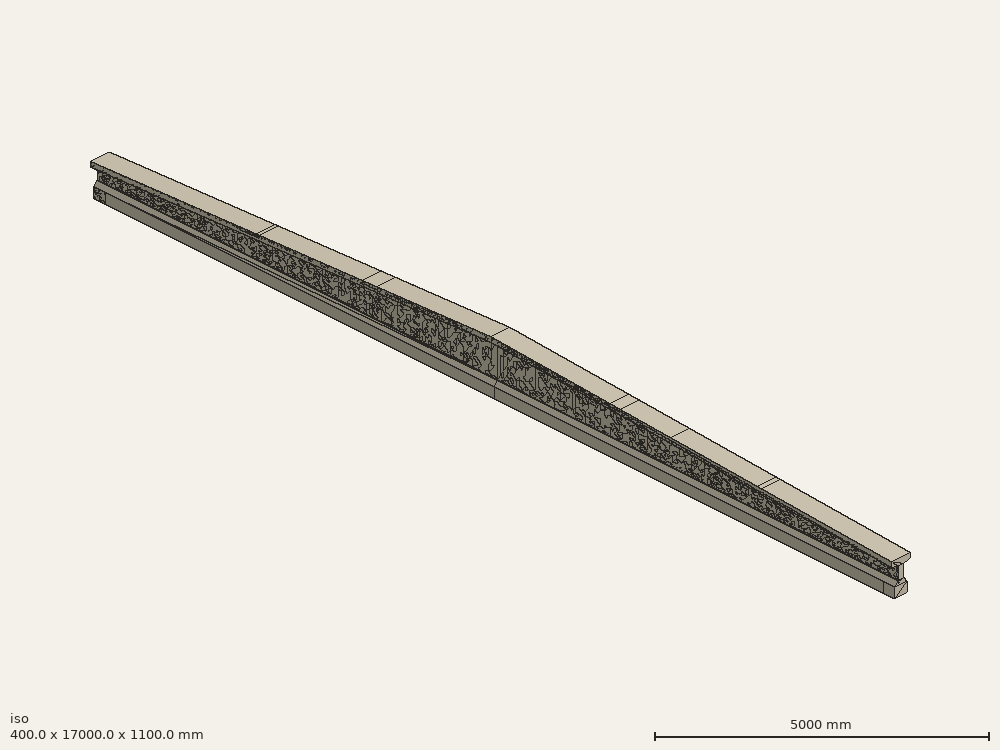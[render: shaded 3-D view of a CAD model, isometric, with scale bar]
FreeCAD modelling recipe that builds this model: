
FCSTD DOCUMENT  (FreeCAD 0.21R33694 (Git))
Label: LGH_3002_beam_2
License: All rights reserved
LicenseURL: http://en.wikipedia.org/wiki/All_rights_reserved
objects: Part::FeaturePython×14, Part::Feature×13, Part::Part2DObjectPython×8, App::MaterialObjectPython×4, Sketcher::SketchObject×3, Part::Compound×2, Fem::ConstraintDisplacement×2, Fem::ConstraintForce×2, Fem::FemSolverObjectPython×1, Part::Loft×1, Part::Extrusion×1, Part::Plane×1, Fem::FemMeshObjectPython×1, Fem::FemAnalysis×1
note: 43 computed .brp shape members not serialized (recipe doc carries the construction recipe); baked Part::Feature solids carry a one-line shape summary decoded from their .brp

FEATURE [Fem::FemSolverObjectPython] SolverCcxTools  # FEM object (typed FeaturePython)
  AnalysisType = 0
  BeamShellResultOutput3D = true
  BucklingFactors = 1
  EigenmodeHighLimit = 1000000
  EigenmodeLowLimit = 0
  EigenmodesCount = 10
  GeometricalNonlinearity = 0
  IterationsControlParameterCutb = 0.25,0.5,0.75,0.85,,,1.5,
  IterationsControlParameterIter = 4,8,9,200,10,400,,200,,
  IterationsControlParameterTimeUse = false
  IterationsThermoMechMaximum = 2000
  IterationsUserDefinedIncrementations = false
  IterationsUserDefinedTimeStepLength = false
  MaterialNonlinearity = 0
  MatrixSolverType = 0
  SplitInputWriter = true
  ThermoMechSteadyState = true
  TimeEnd = 1
  TimeInitialStep = 0.01
FEATURE [Part::Feature] Solid002  label="pad2"
  shape: bbox 400 x 8500 x 530 mm, 6 faces (baked)
FEATURE [Part::Feature] Solid003  label="pad1"
  shape: bbox 400 x 8500 x 530 mm, 6 faces (baked)
FEATURE [Part::Feature] Solid006  label="pad3"
  shape: bbox 400 x 8500 x 530 mm, 6 faces (baked)
FEATURE [Part::Feature] Solid007  label="pad4"
  shape: bbox 400 x 8500 x 530 mm, 6 faces (baked)
FEATURE [Part::Part2DObjectPython] Line  # Draft 2D object (typed FeaturePython)
  Area = 0
  ChamferSize = 0
  Closed = false
  End = (60,8500,970)
  FilletRadius = 0
  Length = 120
  MakeFace = true
  Placement = pos=(-60,8500,970) rot=(0.819793,0.571689,-0.033324;1.73245rad)
  Points = (2) [(0,0,0),(74.3136,69.2385,63.9025)]
  Start = (-60,8500,970)
  Subdivisions = 0
FEATURE [Part::Part2DObjectPython] Line001  # Draft 2D object (typed FeaturePython)
  Area = 0
  ChamferSize = 0
  Closed = false
  End = (60,17000,540)
  FilletRadius = 0
  Length = 8510.87
  MakeFace = true
  Placement = pos=(60,8500,970) rot=(0.819793,0.571689,-0.033324;1.73245rad)
  Points = (2) [(0,0,0),(4601.54,1518.69,-6996.74)]
  Start = (60,8500,970)
  Subdivisions = 0
FEATURE [Part::Part2DObjectPython] Line002  # Draft 2D object (typed FeaturePython)
  Area = 0
  ChamferSize = 0
  Closed = false
  End = (-60,17000,540)
  FilletRadius = 0
  Length = 120
  MakeFace = true
  Placement = pos=(60,17000,540) rot=(0.316109,0.658255,0.683209;2.4861rad)
  Points = (2) [(0,0,0),(73.6331,5.20958,-94.6099)]
  Start = (60,17000,540)
  Subdivisions = 0
FEATURE [Part::Part2DObjectPython] Line003  # Draft 2D object (typed FeaturePython)
  Area = 0
  ChamferSize = 0
  Closed = false
  End = (-60,8500,970)
  FilletRadius = 0
  Length = 8510.87
  MakeFace = true
  Placement = pos=(-60,17000,540) rot=(-0.233099,0.743064,0.627312;3.31022rad)
  Points = (2) [(0,0,0),(3747.29,-525.601,-7623.42)]
  Start = (-60,17000,540)
  Subdivisions = 0
FEATURE [Part::Part2DObjectPython] Line004  # Draft 2D object (typed FeaturePython)
  Area = 0
  ChamferSize = 0
  Closed = false
  End = (-60,17000,290)
  FilletRadius = 0
  Length = 120
  MakeFace = true
  Placement = pos=(60,17000,290) rot=(0.094723,0.678944,0.728054;2.81253rad)
  Points = (2) [(0,0,0),(111.466,13.2123,-42.4359)]
  Start = (60,17000,290)
  Subdivisions = 0
FEATURE [Part::Part2DObjectPython] Line005  # Draft 2D object (typed FeaturePython)
  Area = 0
  ChamferSize = 0
  Closed = false
  End = (-60,8500,290)
  FilletRadius = 0
  Length = 8500
  MakeFace = true
  Placement = pos=(-60,17000,290) rot=(0.929676,0.114122,-0.350256;1.59671rad)
  Points = (2) [(0,0,0),(2050.99,106.63,8248.16)]
  Start = (-60,17000,290)
  Subdivisions = 0
FEATURE [Part::Part2DObjectPython] Line006  # Draft 2D object (typed FeaturePython)
  Area = 0
  ChamferSize = 0
  Closed = false
  End = (60,8500,290)
  FilletRadius = 0
  Length = 120
  MakeFace = true
  Placement = pos=(-60,8500,290) rot=(0.929676,0.114122,-0.350256;1.59671rad)
  Points = (2) [(0,0,0),(103.294,55.0781,-26.3971)]
  Start = (-60,8500,290)
  Subdivisions = 0
FEATURE [Part::Part2DObjectPython] Line007  # Draft 2D object (typed FeaturePython)
  Area = 0
  ChamferSize = 0
  Closed = false
  End = (60,17000,290)
  FilletRadius = 0
  Length = 8500
  MakeFace = true
  Placement = pos=(60,8500,290) rot=(0.895286,0.437229,-0.085401;1.72603rad)
  Points = (2) [(0,0,0),(3124.52,562.012,-7884.89)]
  Start = (60,8500,290)
  Subdivisions = 0
FEATURE [Part::Feature] Solid009  label="web_right"
  shape: bbox 132 x 9350 x 701.5 mm, 6 faces (baked)
FEATURE [Part::Feature] Solid010  label="top_flange_right"
  shape: bbox 400 x 9350 x 581.5 mm, 16 faces (baked)
FEATURE [Part::Feature] Solid012  label="web_left"
  shape: bbox 132 x 9350 x 701.5 mm, 6 faces (baked)
FEATURE [Part::Feature] Solid013  label="top_flange_left"
  shape: bbox 400 x 9350 x 581.5 mm, 16 faces (baked)
FEATURE [Part::Compound] Compound002  label="lines_cut_planes_web"
  Links = -> [Line,Line001,Line002,Line003,Line004,Line005,Line006,Line007]
FEATURE [Part::Feature] Loft010  label="beam_right"
  Placement = pos=(1.041e-12,17000,0) rot=(0,0,1;3.14159rad)
  shape: bbox 400 x 8500 x 1100 mm, 14 faces (baked)
FEATURE [Sketcher::SketchObject] Sketch019
  FullyConstrained = true
  Placement = pos=(0,0,0) rot=(1,0,0;1.5708rad)
  sketch-geometry (12):
    g0: LineSegment StartX=-130 StartY=0 StartZ=0 EndX=130 EndY=4e-16 EndZ=0
    g1: LineSegment StartX=130 StartY=4e-16 StartZ=0 EndX=130 EndY=200 EndZ=0
    g2: LineSegment StartX=130 StartY=200 StartZ=0 EndX=60 EndY=290 EndZ=0
    g3: LineSegment StartX=60 StartY=290 StartZ=0 EndX=60 EndY=540 EndZ=0
    g4: LineSegment StartX=60 StartY=540 StartZ=0 EndX=200 EndY=570 EndZ=0
    g5: LineSegment StartX=200 StartY=570 StartZ=0 EndX=200 EndY=670 EndZ=0
    g6: LineSegment StartX=200 StartY=670 StartZ=0 EndX=-200 EndY=670 EndZ=0
    g7: LineSegment StartX=-200 StartY=670 StartZ=0 EndX=-200 EndY=570 EndZ=0
    g8: LineSegment StartX=-200 StartY=570 StartZ=0 EndX=-60 EndY=540 EndZ=0
    g9: LineSegment StartX=-60 StartY=540 StartZ=0 EndX=-60 EndY=290 EndZ=0
    g10: LineSegment StartX=-60 StartY=290 StartZ=0 EndX=-130 EndY=200 EndZ=0
    g11: LineSegment StartX=-130 StartY=200 StartZ=0 EndX=-130 EndY=0 EndZ=0
  constraints (33):
    c: PointOnObject(g0,g-1)
    c: Symmetric(g0,g0,g-2)
    c: DistanceX(g0,g0) = 260
    c: Coincident(g0,g1)
    c: Vertical(g1)
    c: Coincident(g1,g2)
    c: Coincident(g2,g3)
    c: Vertical(g3)
    c: Coincident(g3,g4)
    c: Coincident(g4,g5)
    c: Vertical(g5)
    c: Coincident(g5,g6)
    c: Coincident(g6,g7)
    c: Vertical(g7)
    c: Coincident(g7,g8)
    c: Coincident(g8,g9)
    c: Vertical(g9)
    c: Coincident(g9,g10)
    c: Coincident(g10,g11)
    c: Coincident(g11,g0)
    c: Vertical(g11)
    c: Equal(g11,g1)
    c: Symmetric(g9,g2,g-2)
    c: Equal(g9,g3)
    c: Symmetric(g6,g5,g-2)
    c: DistanceX(g6,g6) = 400
    c: DistanceY(g0,g5) = 670
    c: Equal(g7,g5)
    c: DistanceX(g9,g2) = 120
    c: DistanceY(g5,g5) = 100
    c: DistanceY(g3,g4) = 30
    c: DistanceY(g1,g1) = 200
    c: DistanceY(g1,g2) = 90
FEATURE [Sketcher::SketchObject] Sketch020
  FullyConstrained = true
  Placement = pos=(0,8500,0) rot=(1,0,0;1.5708rad)
  sketch-geometry (12):
    g0: LineSegment StartX=-130 StartY=0 StartZ=0 EndX=130 EndY=0 EndZ=0
    g1: LineSegment StartX=130 StartY=0 StartZ=0 EndX=130 EndY=200 EndZ=0
    g2: LineSegment StartX=130 StartY=200 StartZ=0 EndX=60 EndY=290 EndZ=0
    g3: LineSegment StartX=60 StartY=290 StartZ=0 EndX=60 EndY=970 EndZ=0
    g4: LineSegment StartX=60 StartY=970 StartZ=0 EndX=200 EndY=1000 EndZ=0
    g5: LineSegment StartX=200 StartY=1000 StartZ=0 EndX=200 EndY=1100 EndZ=0
    g6: LineSegment StartX=200 StartY=1100 StartZ=0 EndX=-200 EndY=1100 EndZ=0
    g7: LineSegment StartX=-200 StartY=1100 StartZ=0 EndX=-200 EndY=1000 EndZ=0
    g8: LineSegment StartX=-200 StartY=1000 StartZ=0 EndX=-60 EndY=970 EndZ=0
    g9: LineSegment StartX=-60 StartY=970 StartZ=0 EndX=-60 EndY=290 EndZ=0
    g10: LineSegment StartX=-60 StartY=290 StartZ=0 EndX=-130 EndY=200 EndZ=0
    g11: LineSegment StartX=-130 StartY=200 StartZ=0 EndX=-130 EndY=0 EndZ=0
  constraints (33):
    c: PointOnObject(g0,g-1)
    c: Symmetric(g0,g0,g-2)
    c: DistanceX(g0,g0) = 260
    c: Coincident(g0,g1)
    c: Vertical(g1)
    c: Coincident(g1,g2)
    c: Coincident(g2,g3)
    c: Vertical(g3)
    c: Coincident(g3,g4)
    c: Coincident(g4,g5)
    c: Vertical(g5)
    c: Coincident(g5,g6)
    c: Coincident(g6,g7)
    c: Vertical(g7)
    c: Coincident(g7,g8)
    c: Coincident(g8,g9)
    c: Vertical(g9)
    c: Coincident(g9,g10)
    c: Coincident(g10,g11)
    c: Coincident(g11,g0)
    c: Vertical(g11)
    c: Equal(g11,g1)
    c: Symmetric(g9,g2,g-2)
    c: Equal(g9,g3)
    c: Symmetric(g6,g5,g-2)
    c: DistanceX(g6,g6) = 400
    c: DistanceY(g0,g5) = 1100
    c: Equal(g7,g5)
    c: DistanceX(g9,g2) = 120
    c: DistanceY(g5,g5) = 100
    c: DistanceY(g3,g4) = 30
    c: DistanceY(g1,g1) = 200
    c: DistanceY(g1,g2) = 90
FEATURE [Part::Loft] Loft009  label="beam_left"
  Closed = false
  MaxDegree = 5
  Ruled = false
  Sections = -> [Sketch019,Sketch020]
  Solid = true
FEATURE [Sketcher::SketchObject] Sketch
  ExternalGeometry = -> [Loft009]
  FullyConstrained = true
  MapMode = 5
  Placement = pos=(0,0,0) rot=(1,0,0;1.5708rad)
  Support = -> [Loft009]
  sketch-geometry (4):
    g0: LineSegment StartX=-130 StartY=0 StartZ=0 EndX=130 EndY=0 EndZ=0
    g1: LineSegment StartX=130 StartY=0 StartZ=0 EndX=130 EndY=200 EndZ=0
    g2: LineSegment StartX=130 StartY=200 StartZ=0 EndX=-130 EndY=200 EndZ=0
    g3: LineSegment StartX=-130 StartY=200 StartZ=0 EndX=-130 EndY=0 EndZ=0
  constraints (10):
    c: Coincident(g0,g1)
    c: Coincident(g1,g2)
    c: Coincident(g2,g3)
    c: Coincident(g3,g0)
    c: Horizontal(g0)
    c: Horizontal(g2)
    c: Vertical(g1)
    c: Vertical(g3)
    c: Coincident(g0,g-3)
    c: Coincident(g1,g-4)
FEATURE [Part::Extrusion] Extrude  label="support_left"
  Base = -> Sketch
  Dir = (0,-1,2e-16)
  DirMode = 2
  FaceMakerClass = Part::FaceMakerBullseye
  LengthFwd = 0
  LengthRev = 250
  Solid = true
  Symmetric = false
FEATURE [Part::FeaturePython] Clone  label="support_right"  # Draft clone (typed FeaturePython)
  AttacherType = Attacher::AttachEngine3D
  Fuse = false
  Objects = -> [Extrude]
  Placement = pos=(0,16750,0) rot=(0,0,1;0rad)
  Scale = (1,1,1)
FEATURE [Part::Plane] Plane003
  AttacherType = Attacher::AttachEngine3D
  Length = 20000
  Placement = pos=(150,0,290) rot=(0,0,1;1.5708rad)
  Width = 300
FEATURE [Part::FeaturePython] Slice  # WARN: FeaturePython — macro-defined, semantics opaque (R4)
  Base = -> Loft009
  Mode = 1
  Tolerance = 0
  Tools = -> [Plane003]
FEATURE [Part::FeaturePython] Slice_child0  label="Slice.0"  # WARN: FeaturePython — macro-defined, semantics opaque (R4)
  Base = -> Slice
  FilterType = 1
  Invert = false
  OverrideMaxVal = 0
  WindowFrom = 80
  WindowTo = 100
  items = 0
FEATURE [Part::FeaturePython] Slice_child1  label="Slice.1"  # WARN: FeaturePython — macro-defined, semantics opaque (R4)
  Base = -> Slice
  FilterType = 1
  Invert = false
  OverrideMaxVal = 0
  WindowFrom = 80
  WindowTo = 100
  items = 1
FEATURE [Part::FeaturePython] Slice001  # WARN: FeaturePython — macro-defined, semantics opaque (R4)
  Base = -> Loft010
  Mode = 1
  Tolerance = 0
  Tools = -> [Plane003]
FEATURE [Part::FeaturePython] Slice001_child0  label="Slice001.0"  # WARN: FeaturePython — macro-defined, semantics opaque (R4)
  Base = -> Slice001
  FilterType = 1
  Invert = false
  OverrideMaxVal = 0
  WindowFrom = 80
  WindowTo = 100
  items = 0
FEATURE [Part::FeaturePython] Slice001_child1  label="Slice001.1"  # WARN: FeaturePython — macro-defined, semantics opaque (R4)
  Base = -> Slice001
  FilterType = 1
  Invert = false
  OverrideMaxVal = 0
  WindowFrom = 80
  WindowTo = 100
  items = 1
FEATURE [Part::FeaturePython] Slice002  # WARN: FeaturePython — macro-defined, semantics opaque (R4)
  Base = -> Slice_child0
  Mode = 1
  Tolerance = 0
  Tools = -> [Extrude]
FEATURE [Part::FeaturePython] Slice002_child0  label="Slice002.0"  # WARN: FeaturePython — macro-defined, semantics opaque (R4)
  Base = -> Slice002
  FilterType = 1
  Invert = false
  OverrideMaxVal = 0
  WindowFrom = 80
  WindowTo = 100
  items = 0
FEATURE [Part::FeaturePython] Slice002_child1  label="Slice002.1"  # WARN: FeaturePython — macro-defined, semantics opaque (R4)
  Base = -> Slice002
  FilterType = 1
  Invert = false
  OverrideMaxVal = 0
  WindowFrom = 80
  WindowTo = 100
  items = 1
FEATURE [Part::FeaturePython] Slice003  # WARN: FeaturePython — macro-defined, semantics opaque (R4)
  Base = -> Slice001_child0
  Mode = 1
  Tolerance = 0
  Tools = -> [Clone]
FEATURE [Part::FeaturePython] Slice003_child0  label="Slice003.0"  # WARN: FeaturePython — macro-defined, semantics opaque (R4)
  Base = -> Slice003
  FilterType = 1
  Invert = false
  OverrideMaxVal = 0
  WindowFrom = 80
  WindowTo = 100
  items = 0
FEATURE [Part::FeaturePython] Slice003_child1  label="Slice003.1"  # WARN: FeaturePython — macro-defined, semantics opaque (R4)
  Base = -> Slice003
  FilterType = 1
  Invert = false
  OverrideMaxVal = 0
  WindowFrom = 80
  WindowTo = 100
  items = 1
FEATURE [Part::Feature] Solid  label="support_left001"
  shape: bbox 260 x 250 x 200 mm, 6 faces (baked)
FEATURE [Fem::ConstraintDisplacement] ConstraintDisplacement  label="left_support"
  NormalDirection = (0,0,-1)
  Normals = (4) [(0,0,-1),(0,0,-1),(0,0,-1),(0,0,-1)]
  Points = (4) [(-130,0,0),(-43.3333,0,0),(43.3333,0,0),(130,0,0)]
  References = -> [Solid]
  Scale = 17
  hasXFormula = false
  hasYFormula = false
  hasZFormula = false
  rotxFix = false
  rotxFree = true
  rotyFix = false
  rotyFree = true
  rotzFix = false
  rotzFree = true
  useFlowSurfaceForce = false
  xDisplacement = 0
  xFix = true
  xFree = false
  xRotation = 0
  yDisplacement = 0
  yFix = true
  yFree = false
  yRotation = 0
  zDisplacement = 0
  zFix = true
  zFree = false
  zRotation = 0
FEATURE [Fem::ConstraintForce] ConstraintForce002  label="prestress1(p)"
  DirectionVector = (0,1,-2e-16)
  Force = 900000
  NormalDirection = (0,-1,2e-16)
  Points = (4) [(26.4133,7.10905e-15,32.3139),(69.7586,2.64699e-14,120.318),(-69.7586,1.75301e-14,79.6821),(-26.4133,3.6891e-14,167.686)]
  References = -> [Solid]
  Reversed = true
  Scale = 19
FEATURE [Part::Feature] Solid014  label="bottom_flange_left"
  shape: bbox 260 x 8500 x 290 mm, 10 faces (baked)
FEATURE [Part::Feature] Solid015  label="support_right001"
  shape: bbox 260 x 250 x 200 mm, 6 faces (baked)
FEATURE [Fem::ConstraintDisplacement] ConstraintDisplacement001  label="right_support"
  NormalDirection = (0,1,-2e-16)
  Normals = (4) [(0,1,-2e-16),(0,1,-2e-16),(0,1,-2e-16),(0,1,-2e-16)]
  Points = (4) [(130,17000,0),(43.3333,17000,0),(-43.3333,17000,0),(-130,17000,0)]
  References = -> [Solid015]
  Scale = 17
  hasXFormula = false
  hasYFormula = false
  hasZFormula = false
  rotxFix = false
  rotxFree = true
  rotyFix = false
  rotyFree = true
  rotzFix = false
  rotzFree = true
  useFlowSurfaceForce = false
  xDisplacement = 0
  xFix = true
  xFree = false
  xRotation = 0
  yDisplacement = 0
  yFix = false
  yFree = true
  yRotation = 0
  zDisplacement = 0
  zFix = true
  zFree = false
  zRotation = 0
FEATURE [Fem::ConstraintForce] ConstraintForce003  label="prestress2(p)"
  DirectionVector = (0,-1,2e-16)
  Force = 900000
  NormalDirection = (0,1,-2e-16)
  Points = (4) [(-26.4133,17000,32.3139),(-69.7586,17000,120.318),(69.7586,17000,79.6821),(26.4133,17000,167.686)]
  References = -> [Solid015]
  Reversed = true
  Scale = 19
FEATURE [Part::Feature] Solid016  label="bottom_flange_right"
  shape: bbox 260 x 8500 x 290 mm, 10 faces (baked)
FEATURE [Part::Compound] Compound  label="slices"
  Links = -> [Slice_child1,Slice001_child1,Slice002_child0,Slice002_child1,Slice003_child0,Slice003_child1]
FEATURE [Part::FeaturePython] BooleanFragments  # WARN: FeaturePython — macro-defined, semantics opaque (R4)
  Mode = 2
  Objects = -> [Solid002,Solid003,Solid006,Solid007,Solid009,Solid010,Solid012,Solid013,Solid,Solid014,Solid015,Solid016]
  Tolerance = 0
FEATURE [App::MaterialObjectPython] MaterialSolid  label="bottom_flange"  # material (typed FeaturePython)
  Category = 0
  Material = AngleOfFriction=30 deg,AuthorAndLicense=(c) 2019 Bernd Hahnebach (CC-BY 3.0),CardName=Concrete-EN-C35_45,CompressiveStrength=15.75 MPa,+7 more (map truncated)
  References = -> [BooleanFragments]
FEATURE [App::MaterialObjectPython] MaterialSolid001  label="top_flange"  # material (typed FeaturePython)
  Category = 0
  Material = AngleOfFriction=30 deg,AuthorAndLicense=(c) 2019 Bernd Hahnebach (CC-BY 3.0),CardName=Concrete-EN-C35_45,CompressiveStrength=15.75 MPa,+7 more (map truncated)
  References = -> [BooleanFragments]
FEATURE [App::MaterialObjectPython] MaterialSolid002  label="web"  # material (typed FeaturePython)
  Category = 0
  Material = AngleOfFriction=30 deg,AuthorAndLicense=(c) 2019 Bernd Hahnebach (CC-BY 3.0),CardName=Concrete-EN-C35_45,CompressiveStrength=15.75 MPa,+7 more (map truncated)
  References = -> [BooleanFragments]
FEATURE [App::MaterialObjectPython] MaterialSolid003  label="supports"  # material (typed FeaturePython)
  Category = 0
  Material = AuthorAndLicense=(c) 2013 Juergen Riegel (CC-BY 3.0),CardName=Steel-Generic,Density=7900 kg/m^3,+9 more (map truncated)
  References = -> [BooleanFragments]
FEATURE [Fem::FemMeshObjectPython] FEMMeshGmsh  # FEM object (typed FeaturePython)
  Algorithm2D = 0
  Algorithm3D = 0
  CharacteristicLengthMax = 0
  CharacteristicLengthMin = 0
  CoherenceMesh = true
  ElementDimension = 0
  ElementOrder = 1
  GeometryTolerance = 1e-06
  GroupsOfNodes = false
  HighOrderOptimize = 0
  MeshSizeFromCurvature = 12
  OptimizeNetgen = false
  OptimizeStd = true
  Part = -> BooleanFragments
  RecombinationAlgorithm = 0
  Recombine3DAll = false
  RecombineAll = false
  SecondOrderLinear = false
FEATURE [Fem::FemAnalysis] Analysis
  Group = -> [SolverCcxTools,ConstraintDisplacement,ConstraintDisplacement001,ConstraintForce002,ConstraintForce003,MaterialSolid,MaterialSolid001,MaterialSolid002,MaterialSolid003,FEMMeshGmsh]
